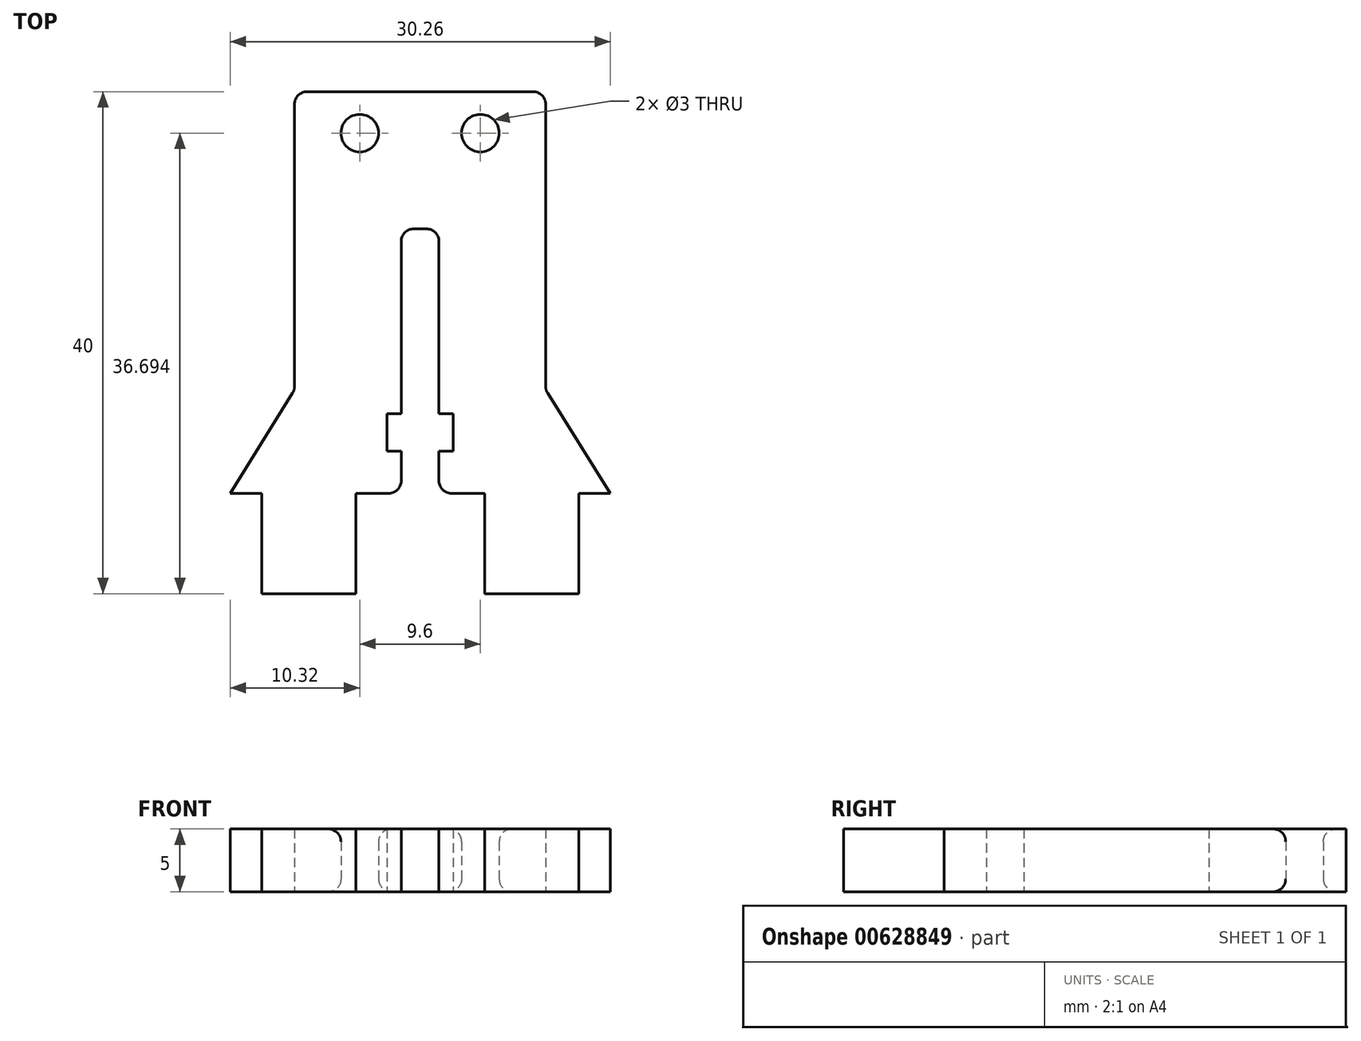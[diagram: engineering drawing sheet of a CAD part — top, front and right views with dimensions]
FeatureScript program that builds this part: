
annotation { "Feature Type Name" : "Feature", "Feature Type Description" : "" }
export const myFeature = defineFeature(function(context is Context, id is Id, definition is map)
    precondition{}
    {
        {
            var Q0;
            Q0=qCreatedBy(makeId("Top.planeOp"),FACE);
            var sketch = newSketch(context, id + "F0", { "sketchPlane" : qUnion([Q0])});
            skLineSegment(sketch, "E0", {"start": v(-12.62, -23.03) * mm, "end": v(-5.12, -23.03) * mm});
            skLineSegment(sketch, "E1", {"start": v(12.64, -23.03) * mm, "end": v(5.14, -23.03) * mm});
            skLineSegment(sketch, "E2", {"start": v(-12.62, -23.03) * mm, "end": v(-12.62, -15.03) * mm});
            skLineSegment(sketch, "E3", {"start": v(-5.12, -23.03) * mm, "end": v(-5.12, -15.03) * mm});
            skLineSegment(sketch, "E4", {"start": v(5.14, -23.03) * mm, "end": v(5.14, -15.03) * mm});
            skLineSegment(sketch, "E5", {"start": v(12.64, -23.03) * mm, "end": v(12.64, -15.03) * mm});
            skLineSegment(sketch, "E6", {"start": v(-12.62, -15.03) * mm, "end": v(-15.12, -15.03) * mm});
            skLineSegment(sketch, "E7", {"start": v(12.64, -15.03) * mm, "end": v(15.14, -15.03) * mm});
            skLineSegment(sketch, "E8", {"start": v(-1.5, -15.03) * mm, "end": v(-1.5, -11.68) * mm});
            skLineSegment(sketch, "E9", {"start": v(1.5, -15.03) * mm, "end": v(1.5, -11.68) * mm});
            skLineSegment(sketch, "E10", {"start": v(-1.5, 6.04) * mm, "end": v(1.5, 6.04) * mm});
            skLineSegment(sketch, "E11", {"start": v(-10, 16.97) * mm, "end": v(10, 16.97) * mm});
            skLineSegment(sketch, "E12", {"start": v(-10, 16.97) * mm, "end": v(-10, -6.81) * mm});
            skLineSegment(sketch, "E13", {"start": v(10, 16.97) * mm, "end": v(10, -6.81) * mm});
            skLineSegment(sketch, "E14", {"start": v(-15.12, -15.03) * mm, "end": v(-10, -6.81) * mm});
            skLineSegment(sketch, "E15", {"start": v(10, -6.81) * mm, "end": v(15.14, -15.03) * mm});
            skLineSegment(sketch, "E16", {"start": v(-2.65, -11.68) * mm, "end": v(-1.5, -11.68) * mm});
            skLineSegment(sketch, "E17", {"start": v(-5.12, -15.03) * mm, "end": v(-1.5, -15.03) * mm});
            skLineSegment(sketch, "E18", {"start": v(1.5, -15.03) * mm, "end": v(5.14, -15.03) * mm});
            skLineSegment(sketch, "E19", {"start": v(-2.65, -8.68) * mm, "end": v(-1.5, -8.68) * mm});
            skLineSegment(sketch, "E20", {"start": v(-2.65, -8.68) * mm, "end": v(-2.65, -11.68) * mm});
            skLineSegment(sketch, "E21", {"start": v(2.65, -8.68) * mm, "end": v(2.65, -11.68) * mm});
            skLineSegment(sketch, "E22.trimOffspring", {"start": v(1.5, -8.68) * mm, "end": v(1.5, 6.04) * mm});
            skLineSegment(sketch, "E23.trimOffspring", {"start": v(-1.5, -8.68) * mm, "end": v(-1.5, 6.04) * mm});
            skLineSegment(sketch, "E24.trimOffspring", {"start": v(1.5, -11.68) * mm, "end": v(2.65, -11.68) * mm});
            skLineSegment(sketch, "E25.trimOffspring", {"start": v(1.5, -8.68) * mm, "end": v(2.65, -8.68) * mm});
            skCircle(sketch, "E26", {"center": v(-4.8, 13.66) * mm, "radius": 1.5 * mm});
            skCircle(sketch, "E27", {"center": v(4.8, 13.66) * mm, "radius": 1.5 * mm});
            skSolve(sketch);
        }
        {
            var Q0;
            Q0=makeQuery(id+"F0.imprint","IMPRINT",FACE,{"disambiguationData":[TD([[makeQuery(id+"F0.imprint","IMPRINT",EDGE,{"derivedFrom":sQuery(id+"F0.wireOp",EDGE,"E0")}),1.0]])]});
            extrude(context, id + "F1", {"entities" : qUnion([Q0]), "depth" : 5 * mm, "offsetDistance" : 25.4 * mm});
        }
        {
            var Q0;
            Q0=makeQuery(id+"F1.opExtrude","SWEPT_EDGE",EDGE,{"disambiguationData":[OSD([sQuery(id+"F0.wireOp",EDGE,"E11"),sQuery(id+"F0.wireOp",EDGE,"E13")])]});
            var Q1;
            Q1=makeQuery(id+"F1.opExtrude","SWEPT_EDGE",EDGE,{"disambiguationData":[OSD([sQuery(id+"F0.wireOp",EDGE,"E13"),sQuery(id+"F0.wireOp",EDGE,"E15")])]});
            var Q2;
            Q2=makeQuery(id+"F1.opExtrude","SWEPT_EDGE",EDGE,{"disambiguationData":[OSD([sQuery(id+"F0.wireOp",EDGE,"E12"),sQuery(id+"F0.wireOp",EDGE,"E14")])]});
            var Q3;
            Q3=makeQuery(id+"F1.opExtrude","SWEPT_EDGE",EDGE,{"disambiguationData":[OSD([sQuery(id+"F0.wireOp",EDGE,"E11"),sQuery(id+"F0.wireOp",EDGE,"E12")])]});
            var Q4;
            Q4=makeQuery(id+"F1.opExtrude","CAP_EDGE",EDGE,{"disambiguationData":[OSD([sQuery(id+"F0.wireOp",EDGE,"E26")])],"isStart":true});
            var Q5;
            Q5=makeQuery(id+"F1.opExtrude","CAP_EDGE",EDGE,{"disambiguationData":[OSD([sQuery(id+"F0.wireOp",EDGE,"E27")])],"isStart":true});
            var Q6;
            Q6=makeQuery(id+"F1.opExtrude","CAP_EDGE",EDGE,{"disambiguationData":[OSD([sQuery(id+"F0.wireOp",EDGE,"E27")])],"isStart":false});
            var Q7;
            Q7=makeQuery(id+"F1.opExtrude","CAP_EDGE",EDGE,{"disambiguationData":[OSD([sQuery(id+"F0.wireOp",EDGE,"E26")])],"isStart":false});
            var Q8;
            Q8=makeQuery(id+"F1.opExtrude","SWEPT_EDGE",EDGE,{"disambiguationData":[OSD([sQuery(id+"F0.wireOp",EDGE,"E9"),sQuery(id+"F0.wireOp",EDGE,"E18")])]});
            var Q9;
            Q9=makeQuery(id+"F1.opExtrude","SWEPT_EDGE",EDGE,{"disambiguationData":[OSD([sQuery(id+"F0.wireOp",EDGE,"E8"),sQuery(id+"F0.wireOp",EDGE,"E17")])]});
            var Q10;
            Q10=makeQuery(id+"F1.opExtrude","SWEPT_EDGE",EDGE,{"disambiguationData":[OSD([sQuery(id+"F0.wireOp",EDGE,"E10"),sQuery(id+"F0.wireOp",EDGE,"E22.trimOffspring")])]});
            var Q11;
            Q11=makeQuery(id+"F1.opExtrude","SWEPT_EDGE",EDGE,{"disambiguationData":[OSD([sQuery(id+"F0.wireOp",EDGE,"E10"),sQuery(id+"F0.wireOp",EDGE,"E23.trimOffspring")])]});
            fillet(context, id + "F2", {"entities" : qUnion([Q0, Q1, Q2, Q3, Q4, Q5, Q6, Q7, Q8, Q9, Q10, Q11]), "radius" : 1 * mm, "tangentPropagation" : true, "allowEdgeOverflow" : false});
        }
    });
